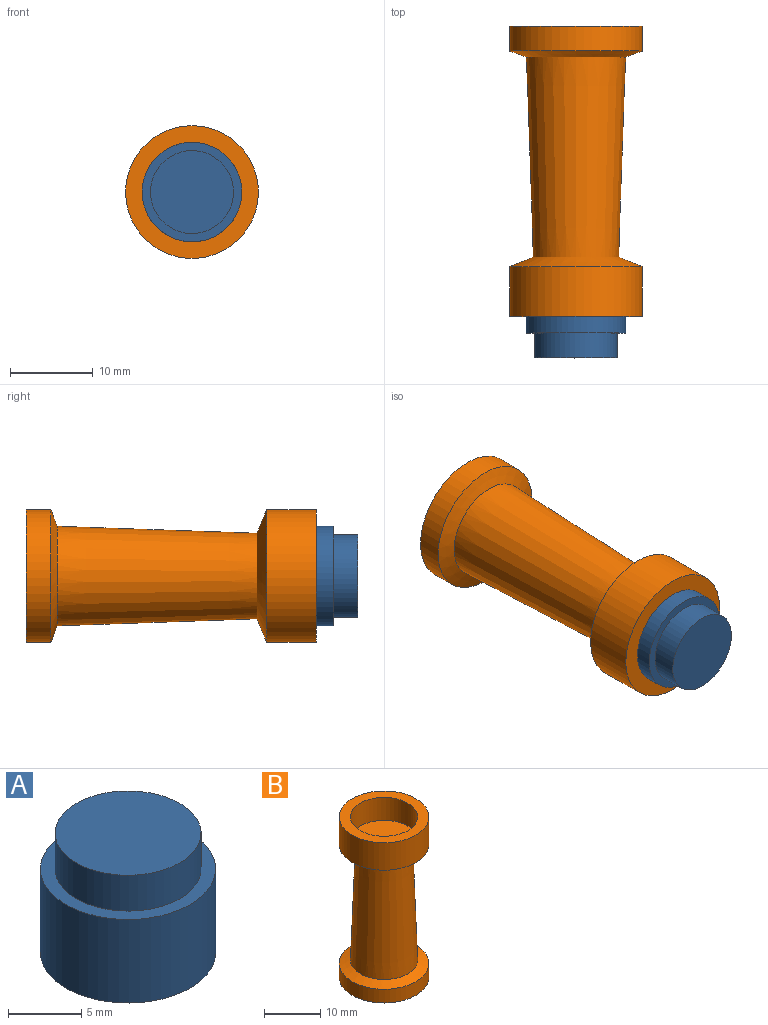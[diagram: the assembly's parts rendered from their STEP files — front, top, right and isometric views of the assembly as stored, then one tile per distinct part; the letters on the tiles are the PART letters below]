
ASSEMBLY  parts=2 mates=1
PART A: 5 faces, bbox 12x12x10 mm
  f0: plane 12x12mm, normal (0,0,-1), area 113.1mm2, adj f1
  f1: cylinder r=6mm len=12mm, axis (0,0,1), area 263.9mm2, adj f0,f2
  f2: plane 12x12mm, normal (0,0,1), area 34.6mm2, adj f1,f3
  f3: cylinder r=5mm len=10mm, axis (0,0,1), area 94.2mm2, adj f2,f4
  f4: plane 10x10mm, normal (0,0,1), area 78.5mm2, adj f3
PART B: 9 faces, bbox 16x16x35 mm
  f0: plane 16x16mm, normal (0,0,-1), area 201.1mm2, adj f1
  f1: cylinder r=8mm len=16mm, axis (0,0,1), area 150.8mm2, adj f0,f2
  f2: cone r=8mm half-angle=70deg, axis (0,0,-1), area 93.6mm2, adj f1,f3
  f3: cone r=6mm half-angle=2deg, axis (0,0,-1), area 846.1mm2, adj f2,f4
  f4: cone r=5.16mm half-angle=68deg, axis (0,0,1), area 126.7mm2, adj f3,f5
  f5: cylinder r=8mm len=16mm, axis (0,0,1), area 301.6mm2, adj f4,f6
  f6: plane 16x16mm, normal (0,0,1), area 88mm2, adj f5,f7
  f7: cylinder r=6mm len=12mm, axis (0,0,1), area 188.5mm2, adj f6,f8
  f8: plane 12x12mm, normal (0,0,1), area 113.1mm2, adj f7
PLACE A rot(axis=(1,0,0),90deg) t=(0,-30,0)mm
PLACE B rot(axis=(0.58,-0.58,0.58),120deg) t=(0,0,0)mm
MATE fastened A.f1 <-> B.f1  axis (0,1,0) through (0,-30,0)mm
